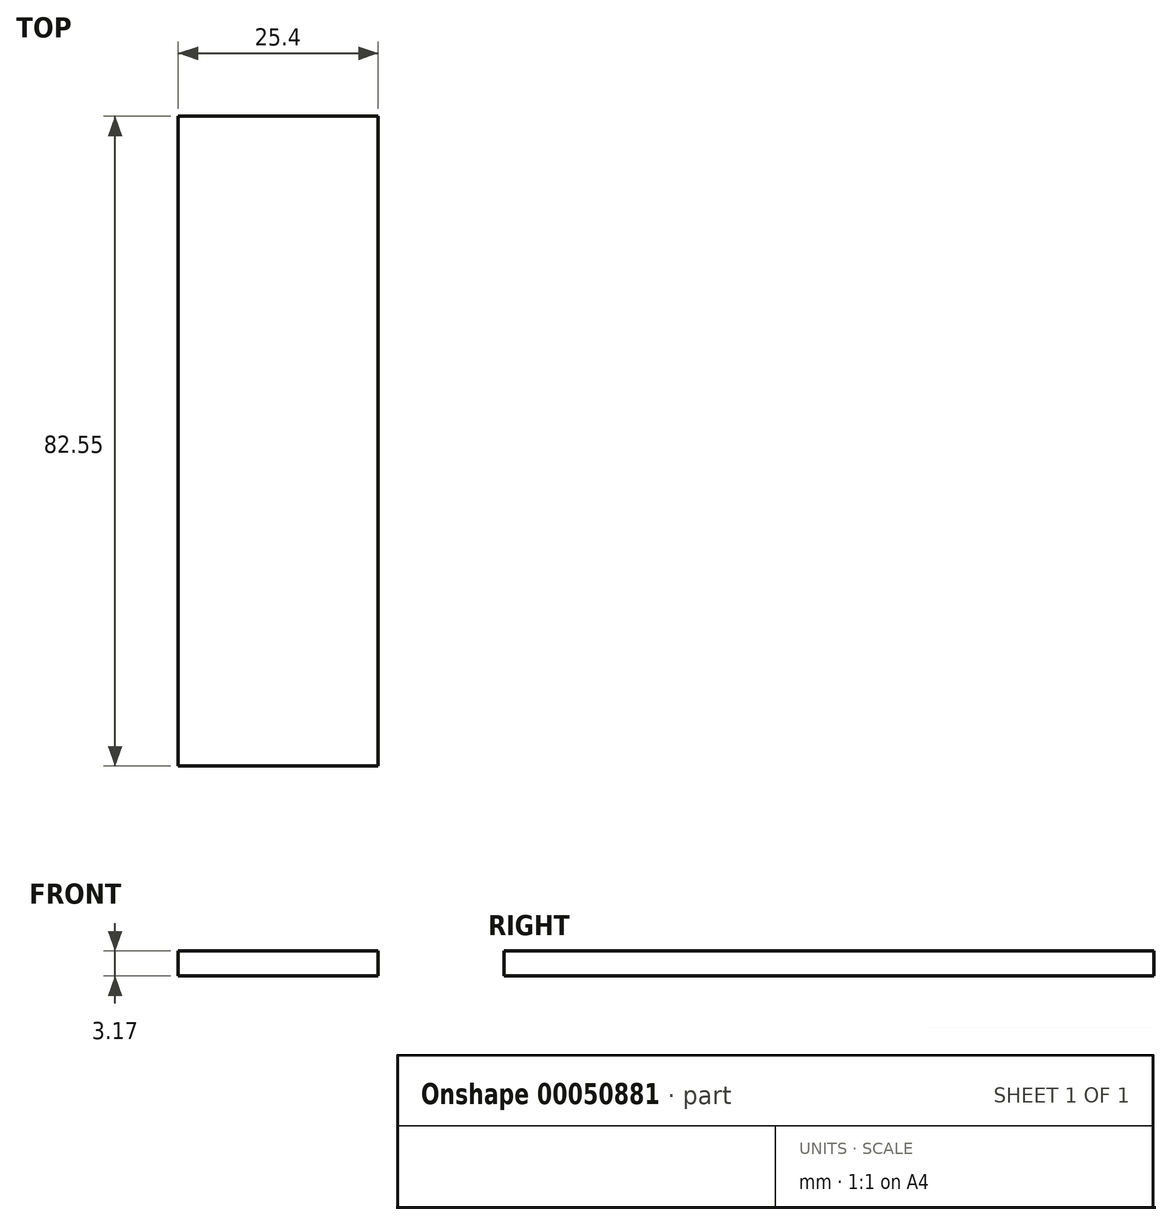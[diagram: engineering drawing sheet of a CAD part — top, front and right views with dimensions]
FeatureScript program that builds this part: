
annotation { "Feature Type Name" : "Feature", "Feature Type Description" : "" }
export const myFeature = defineFeature(function(context is Context, id is Id, definition is map)
    precondition{}
    {
        {
            var Q0;
            Q0=qCreatedBy(makeId("Top.planeOp"),FACE);
            var sketch = newSketch(context, id + "F0", { "sketchPlane" : qUnion([Q0])});
            skLineSegment(sketch, "E0.bottom", {"start": v(-12.21, -37.62) * mm, "end": v(13.19, -37.62) * mm});
            skLineSegment(sketch, "E0.top", {"start": v(-12.21, 44.93) * mm, "end": v(13.19, 44.93) * mm});
            skLineSegment(sketch, "E0.left", {"start": v(-12.21, -37.62) * mm, "end": v(-12.21, 44.93) * mm});
            skLineSegment(sketch, "E0.right", {"start": v(13.19, -37.62) * mm, "end": v(13.19, 44.93) * mm});
            skSolve(sketch);
        }
        {
            var Q0;
            Q0 = qSketchRegion(id + "F0", true);
            extrude(context, id + "F1", {"entities" : qUnion([Q0]), "depth" : 3.17 * mm});
        }
    });
